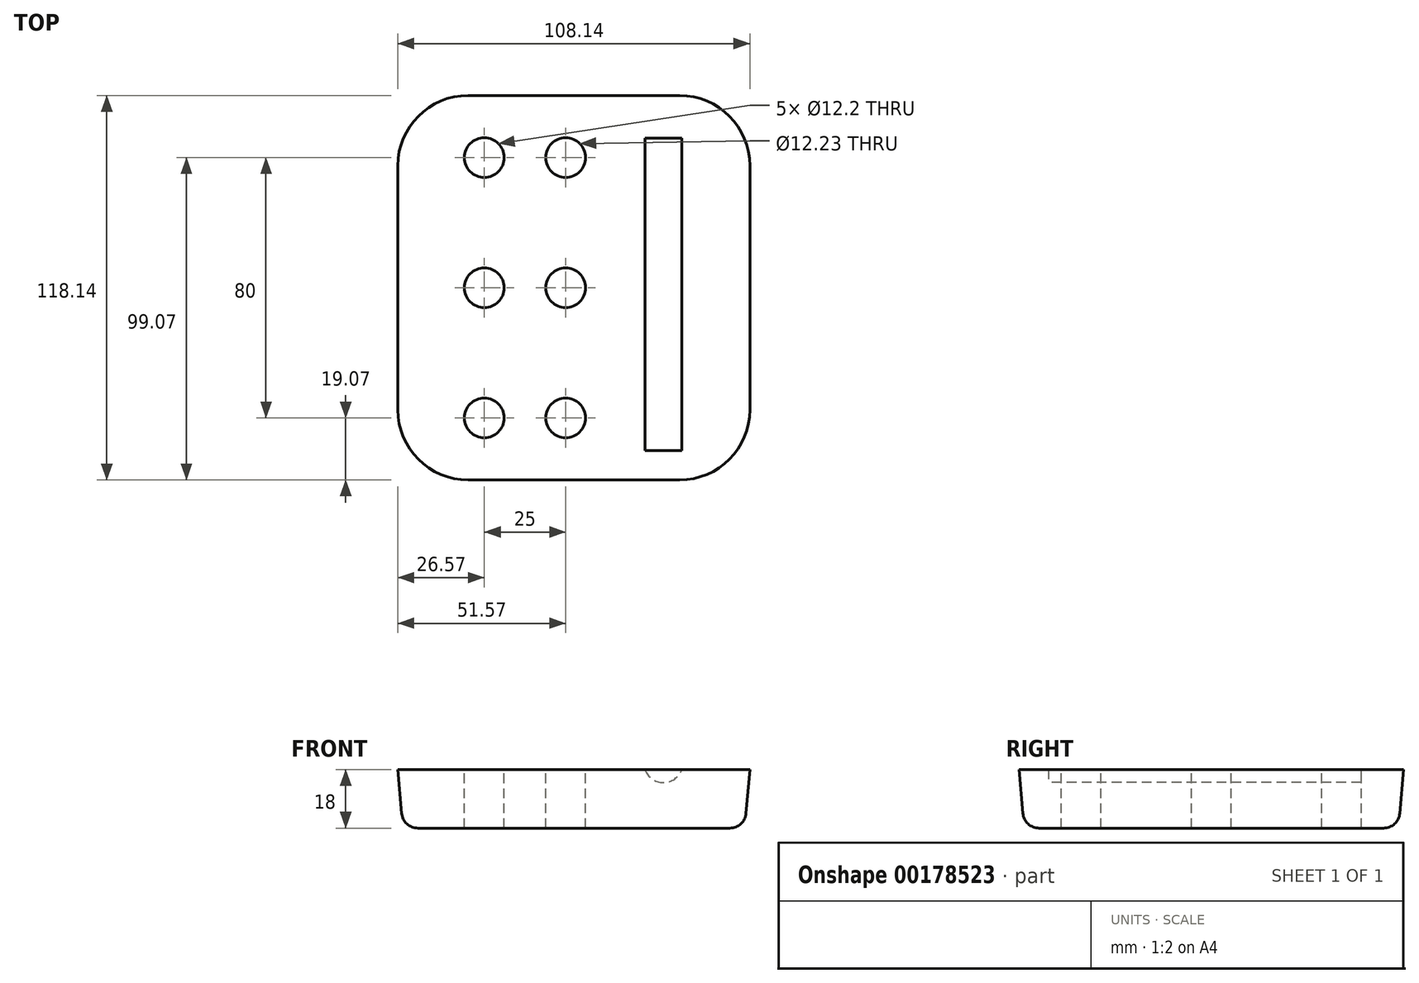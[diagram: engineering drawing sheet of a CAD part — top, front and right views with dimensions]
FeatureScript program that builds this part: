
annotation { "Feature Type Name" : "Feature", "Feature Type Description" : "" }
export const myFeature = defineFeature(function(context is Context, id is Id, definition is map)
    precondition{}
    {
        {
            var Q0;
            Q0=qCreatedBy(makeId("Top.planeOp"),FACE);
            var sketch = newSketch(context, id + "F0", { "sketchPlane" : qUnion([Q0])});
            skLineSegment(sketch, "E0.bottom", {"start": v(20, 0) * mm, "end": v(85, 0) * mm});
            skLineSegment(sketch, "E0.top", {"start": v(20, 115) * mm, "end": v(85, 115) * mm});
            skLineSegment(sketch, "E0.left", {"start": v(0, 20) * mm, "end": v(0, 95) * mm});
            skLineSegment(sketch, "E0.right", {"start": v(105, 20) * mm, "end": v(105, 95) * mm});
            skPoint(sketch, "E1.visualSharp", {"position": v(0, 115) * mm});
            skArc(sketch, "E1.filletArc", {"start": v(20, 115) * mm, "mid": v(5.86, 109.14) * mm, "end": v(0, 95) * mm});
            skPoint(sketch, "E2.visualSharp", {"position": v(105, 115) * mm});
            skArc(sketch, "E2.filletArc", {"start": v(105, 95) * mm, "mid": v(99.14, 109.14) * mm, "end": v(85, 115) * mm});
            skPoint(sketch, "E3.visualSharp", {"position": v(0, 0) * mm});
            skArc(sketch, "E3.filletArc", {"start": v(0, 20) * mm, "mid": v(5.86, 5.86) * mm, "end": v(20, 0) * mm});
            skPoint(sketch, "E4.visualSharp", {"position": v(105, 0) * mm});
            skArc(sketch, "E4.filletArc", {"start": v(85, 0) * mm, "mid": v(99.14, 5.86) * mm, "end": v(105, 20) * mm});
            skSolve(sketch);
        }
        {
            var Q0;
            Q0=makeQuery(id+"F0.imprint","IMPRINT",FACE,{"disambiguationData":[TD([[makeQuery(id+"F0.imprint","IMPRINT",EDGE,{"derivedFrom":sQuery(id+"F0.wireOp",EDGE,"E0.bottom")}),1.0]])]});
            extrude(context, id + "F1", {"entities" : qUnion([Q0]), "depth" : 20 * mm, "hasDraft" : true, "draftAngle" : 5 * degree});
        }
        {
            var Q0;
            Q0=makeQuery(id+"F1.opExtrude","CAP_FACE",FACE,{"disambiguationData":[OSD([sQuery(id+"F0.wireOp",EDGE,"E0.bottom"),sQuery(id+"F0.wireOp",EDGE,"E0.top"),sQuery(id+"F0.wireOp",EDGE,"E0.left"),sQuery(id+"F0.wireOp",EDGE,"E0.right"),sQuery(id+"F0.wireOp",EDGE,"E1.filletArc"),sQuery(id+"F0.wireOp",EDGE,"E2.filletArc"),sQuery(id+"F0.wireOp",EDGE,"E3.filletArc"),sQuery(id+"F0.wireOp",EDGE,"E4.filletArc")])],"isStart":true});
            fillet(context, id + "F2", {"entities" : qUnion([Q0]), "radius" : 5 * mm, "tangentPropagation" : true, "allowEdgeOverflow" : false});
        }
        {
            var Q0;
            Q0=makeQuery(id+"F1.opExtrude","CAP_FACE",FACE,{"disambiguationData":[OSD([sQuery(id+"F0.wireOp",EDGE,"E0.bottom"),sQuery(id+"F0.wireOp",EDGE,"E0.top"),sQuery(id+"F0.wireOp",EDGE,"E0.left"),sQuery(id+"F0.wireOp",EDGE,"E0.right"),sQuery(id+"F0.wireOp",EDGE,"E1.filletArc"),sQuery(id+"F0.wireOp",EDGE,"E2.filletArc"),sQuery(id+"F0.wireOp",EDGE,"E3.filletArc"),sQuery(id+"F0.wireOp",EDGE,"E4.filletArc")])],"isStart":false});
            var sketch = newSketch(context, id + "F3", { "sketchPlane" : qUnion([Q0])});
            skLineSegment(sketch, "E5.bottom", {"start": v(0, 0) * mm, "end": v(25, 0) * mm, "construction": true});
            skLineSegment(sketch, "E5.top", {"start": v(0, 57.5) * mm, "end": v(25, 57.5) * mm, "construction": true});
            skLineSegment(sketch, "E5.left", {"start": v(0, 0) * mm, "end": v(0, 57.5) * mm, "construction": true});
            skLineSegment(sketch, "E5.right", {"start": v(25, 0) * mm, "end": v(25, 57.5) * mm, "construction": true});
            skLineSegment(sketch, "E6", {"start": v(25, 57.5) * mm, "end": v(25, 17.5) * mm, "construction": true});
            skLineSegment(sketch, "E7", {"start": v(25, 17.5) * mm, "end": v(25, 97.5) * mm, "construction": true});
            skLineSegment(sketch, "E8", {"start": v(25, 97.5) * mm, "end": v(50, 97.5) * mm, "construction": true});
            skLineSegment(sketch, "E9", {"start": v(50, 97.5) * mm, "end": v(50, 57.5) * mm, "construction": true});
            skLineSegment(sketch, "E10", {"start": v(50, 57.5) * mm, "end": v(50, 17.5) * mm, "construction": true});
            skCircle(sketch, "E11", {"center": v(25, 97.5) * mm, "radius": 6.1 * mm});
            skCircle(sketch, "E12", {"center": v(25, 57.5) * mm, "radius": 6.1 * mm});
            skCircle(sketch, "E13", {"center": v(25, 17.5) * mm, "radius": 6.1 * mm});
            skCircle(sketch, "E14", {"center": v(50, 17.5) * mm, "radius": 6.1 * mm});
            skCircle(sketch, "E15", {"center": v(50, 57.5) * mm, "radius": 6.1 * mm});
            skCircle(sketch, "E16", {"center": v(50, 97.5) * mm, "radius": 6.12 * mm});
            skSolve(sketch);
        }
        {
            var Q0;
            Q0 = qSketchRegion(id + "F3", true);
            extrude(context, id + "F4", {"entities" : qUnion([Q0]), "operationType" : NewBodyOperationType.REMOVE, "oppositeDirection" : true, "depth" : 25 * mm});
        }
        {
            var Q0;
            Q0=makeQuery(id+"F1.opExtrude","CAP_FACE",FACE,{"disambiguationData":[OSD([sQuery(id+"F0.wireOp",EDGE,"E0.bottom"),sQuery(id+"F0.wireOp",EDGE,"E0.top"),sQuery(id+"F0.wireOp",EDGE,"E0.left"),sQuery(id+"F0.wireOp",EDGE,"E0.right"),sQuery(id+"F0.wireOp",EDGE,"E1.filletArc"),sQuery(id+"F0.wireOp",EDGE,"E2.filletArc"),sQuery(id+"F0.wireOp",EDGE,"E3.filletArc"),sQuery(id+"F0.wireOp",EDGE,"E4.filletArc")])],"isStart":false});
            var sketch = newSketch(context, id + "F5", { "sketchPlane" : qUnion([Q0])});
            skLineSegment(sketch, "E17.bottom", {"start": v(0, 0) * mm, "end": v(80, 0) * mm, "construction": true});
            skLineSegment(sketch, "E17.top", {"start": v(0, 7.5) * mm, "end": v(80, 7.5) * mm, "construction": true});
            skLineSegment(sketch, "E17.left", {"start": v(0, 0) * mm, "end": v(0, 7.5) * mm, "construction": true});
            skLineSegment(sketch, "E17.right", {"start": v(80, 0) * mm, "end": v(80, 7.5) * mm, "construction": true});
            skLineSegment(sketch, "E18.bottom", {"start": v(80, 7.5) * mm, "end": v(74, 7.5) * mm});
            skLineSegment(sketch, "E18.top", {"start": v(80, 103.5) * mm, "end": v(74, 103.5) * mm});
            skLineSegment(sketch, "E18.left", {"start": v(80, 7.5) * mm, "end": v(80, 103.5) * mm});
            skLineSegment(sketch, "E18.right", {"start": v(74, 7.5) * mm, "end": v(74, 103.5) * mm});
            skSolve(sketch);
        }
        {
            var Q0;
            Q0=makeQuery(id+"F5.imprint","IMPRINT",FACE,{"disambiguationData":[TD([[makeQuery(id+"F5.imprint","IMPRINT",EDGE,{"derivedFrom":sQuery(id+"F5.wireOp",EDGE,"E18.bottom")}),-1.0]])]});
            var Q1;
            Q1=sQuery(id+"F5.wireOp",EDGE,"E18.left");
            revolve(context, id + "F6", {"operationType" : NewBodyOperationType.REMOVE, "entities" : qUnion([Q0]), "axis" : qUnion([Q1]), "revolveType" : RevolveType.FULL});
        }
        {
            var Q0;
            Q0=qCreatedBy(makeId("Front.planeOp"),FACE);
            var sketch = newSketch(context, id + "F7", { "sketchPlane" : qUnion([Q0])});
            skLineSegment(sketch, "E19", {"start": v(0, 0) * mm, "end": v(0, 18) * mm, "construction": true});
            skLineSegment(sketch, "E20", {"start": v(0, 18) * mm, "end": v(-10, 18) * mm, "construction": true});
            skLineSegment(sketch, "E21.bottom", {"start": v(-10, 18) * mm, "end": v(112.24, 18) * mm});
            skLineSegment(sketch, "E21.top", {"start": v(-10, 26) * mm, "end": v(112.24, 26) * mm});
            skLineSegment(sketch, "E21.left", {"start": v(-10, 18) * mm, "end": v(-10, 26) * mm});
            skLineSegment(sketch, "E21.right", {"start": v(112.24, 18) * mm, "end": v(112.24, 26) * mm});
            skSolve(sketch);
        }
        {
            var Q0;
            Q0 = qSketchRegion(id + "F7", true);
            extrude(context, id + "F8", {"entities" : qUnion([Q0]), "operationType" : NewBodyOperationType.REMOVE, "endBound" : BoundingType.THROUGH_ALL, "oppositeDirection" : true, "depth" : 150 * mm, "hasSecondDirection" : true, "secondDirectionOppositeDirection" : false, "secondDirectionDepth" : 5 * mm});
        }
    });
